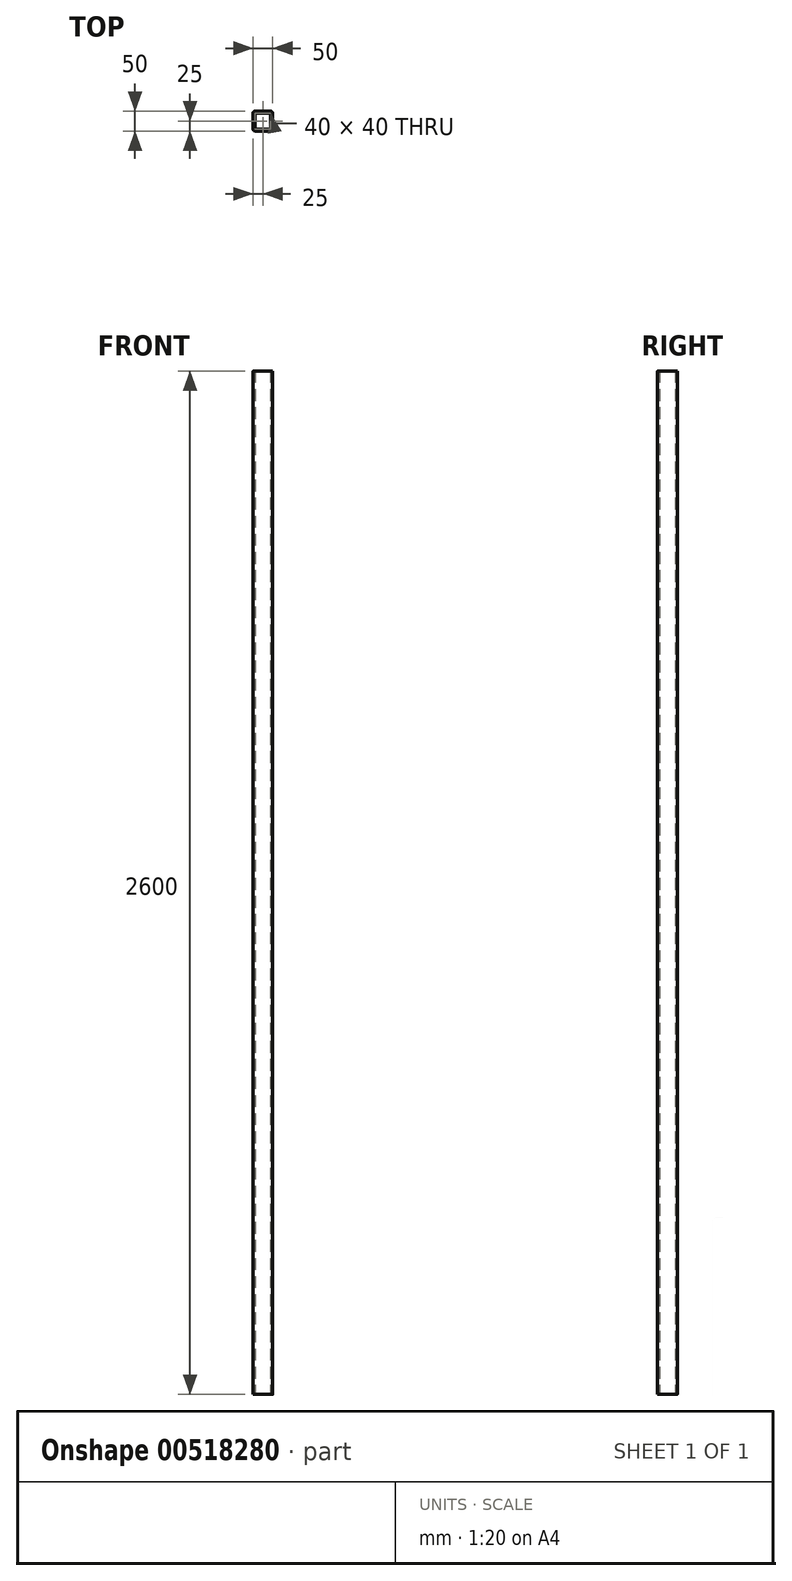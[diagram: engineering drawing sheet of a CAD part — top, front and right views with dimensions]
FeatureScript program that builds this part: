
annotation { "Feature Type Name" : "Feature", "Feature Type Description" : "" }
export const myFeature = defineFeature(function(context is Context, id is Id, definition is map)
    precondition{}
    {
        {
            var Q0;
            Q0=qCreatedBy(makeId("Top.planeOp"),FACE);
            var sketch = newSketch(context, id + "F0", { "sketchPlane" : qUnion([Q0])});
            skLineSegment(sketch, "E0.bottom", {"start": v(20, -25) * mm, "end": v(-20, -25) * mm});
            skLineSegment(sketch, "E0.top", {"start": v(20, 25) * mm, "end": v(-20, 25) * mm});
            skLineSegment(sketch, "E0.left", {"start": v(25, -20) * mm, "end": v(25, 20) * mm});
            skLineSegment(sketch, "E0.right", {"start": v(-25, -20) * mm, "end": v(-25, 20) * mm});
            skPoint(sketch, "E0.middle", {"position": v(0, 0) * mm});
            skLineSegment(sketch, "E1.bottom", {"start": v(20, -20) * mm, "end": v(-20, -20) * mm});
            skLineSegment(sketch, "E1.top", {"start": v(20, 20) * mm, "end": v(-20, 20) * mm});
            skLineSegment(sketch, "E1.left", {"start": v(20, -20) * mm, "end": v(20, 20) * mm});
            skLineSegment(sketch, "E1.right", {"start": v(-20, -20) * mm, "end": v(-20, 20) * mm});
            skPoint(sketch, "E2.visualSharp", {"position": v(-25, 25) * mm});
            skArc(sketch, "E2.filletArc", {"start": v(-20, 25) * mm, "mid": v(-23.54, 23.54) * mm, "end": v(-25, 20) * mm});
            skPoint(sketch, "E3.visualSharp", {"position": v(25, 25) * mm});
            skArc(sketch, "E3.filletArc", {"start": v(25, 20) * mm, "mid": v(23.54, 23.54) * mm, "end": v(20, 25) * mm});
            skPoint(sketch, "E4.visualSharp", {"position": v(-25, -25) * mm});
            skArc(sketch, "E4.filletArc", {"start": v(-25, -20) * mm, "mid": v(-23.54, -23.54) * mm, "end": v(-20, -25) * mm});
            skPoint(sketch, "E5.visualSharp", {"position": v(25, -25) * mm});
            skArc(sketch, "E5.filletArc", {"start": v(20, -25) * mm, "mid": v(23.54, -23.54) * mm, "end": v(25, -20) * mm});
            skSolve(sketch);
        }
        {
            var Q0;
            Q0=qSketchRegion(id+"F0",true);
            extrude(context, id + "F1", {"entities" : qUnion([Q0]), "depth" : 2600 * mm, "offsetDistance" : 25 * mm});
        }
    });
